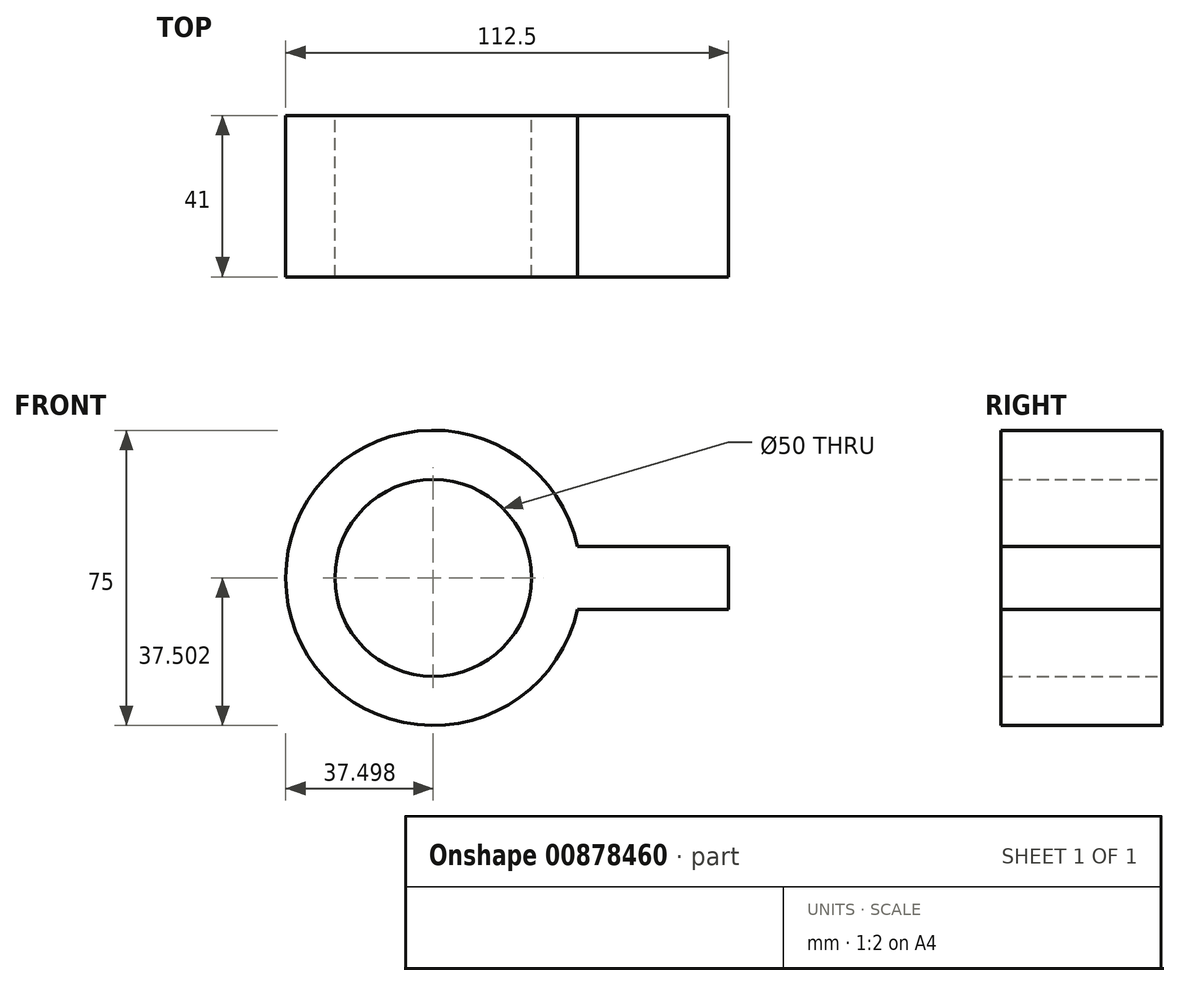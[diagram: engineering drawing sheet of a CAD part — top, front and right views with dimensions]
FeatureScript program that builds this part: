
annotation { "Feature Type Name" : "Feature", "Feature Type Description" : "" }
export const myFeature = defineFeature(function(context is Context, id is Id, definition is map)
    precondition{}
    {
        {
            var Q0;
            Q0=qCreatedBy(makeId("Front.planeOp"),FACE);
            var sketch = newSketch(context, id + "F0", { "sketchPlane" : qUnion([Q0])});
            skCircle(sketch, "E0", {"center": v(-37.33, -12.63) * mm, "radius": 37.5 * mm});
            skCircle(sketch, "E1", {"center": v(-37.33, -12.63) * mm, "radius": 25 * mm});
            skSolve(sketch);
        }
        {
            var Q0;
            Q0 = qSketchRegion(id + "F0", true);
            extrude(context, id + "F1", {"entities" : qUnion([Q0]), "depth" : 41 * mm, "offsetDistance" : 25 * mm});
        }
        {
            var Q0;
            Q0=makeQuery(id+"F1.opExtrude","CAP_FACE",FACE,{"disambiguationData":[OSD([sQuery(id+"F0.wireOp",EDGE,"E0"),sQuery(id+"F0.wireOp",EDGE,"E1")])],"isStart":false});
            var sketch = newSketch(context, id + "F2", { "sketchPlane" : qUnion([Q0])});
            skLineSegment(sketch, "E2", {"start": v(-37.33, 12.37) * mm, "end": v(-37.33, -37.63) * mm});
            skLineSegment(sketch, "E3", {"start": v(37.67, -12.63) * mm, "end": v(37.67, -4.63) * mm});
            skLineSegment(sketch, "E4", {"start": v(37.67, -4.63) * mm, "end": v(37.67, -20.63) * mm});
            skLineSegment(sketch, "E5", {"start": v(37.67, -20.63) * mm, "end": v(-0.7, -20.63) * mm});
            skLineSegment(sketch, "E6", {"start": v(37.67, -4.63) * mm, "end": v(-0.7, -4.63) * mm});
            skSolve(sketch);
        }
        {
            var Q0;
            {var subQ2=sQuery(id+"F2.wireOp",EDGE,"E5");Q0=makeQuery(id+"F2.imprint","IMPRINT",FACE,{"disambiguationData":[TD([[makeQuery(id+"F2.imprint","IMPRINT",EDGE,{"derivedFrom":subQ2}),-1.0]])]});}
            extrude(context, id + "F3", {"entities" : qUnion([Q0]), "operationType" : NewBodyOperationType.ADD, "oppositeDirection" : true, "depth" : 41 * mm, "offsetDistance" : 25 * mm});
        }
    });
